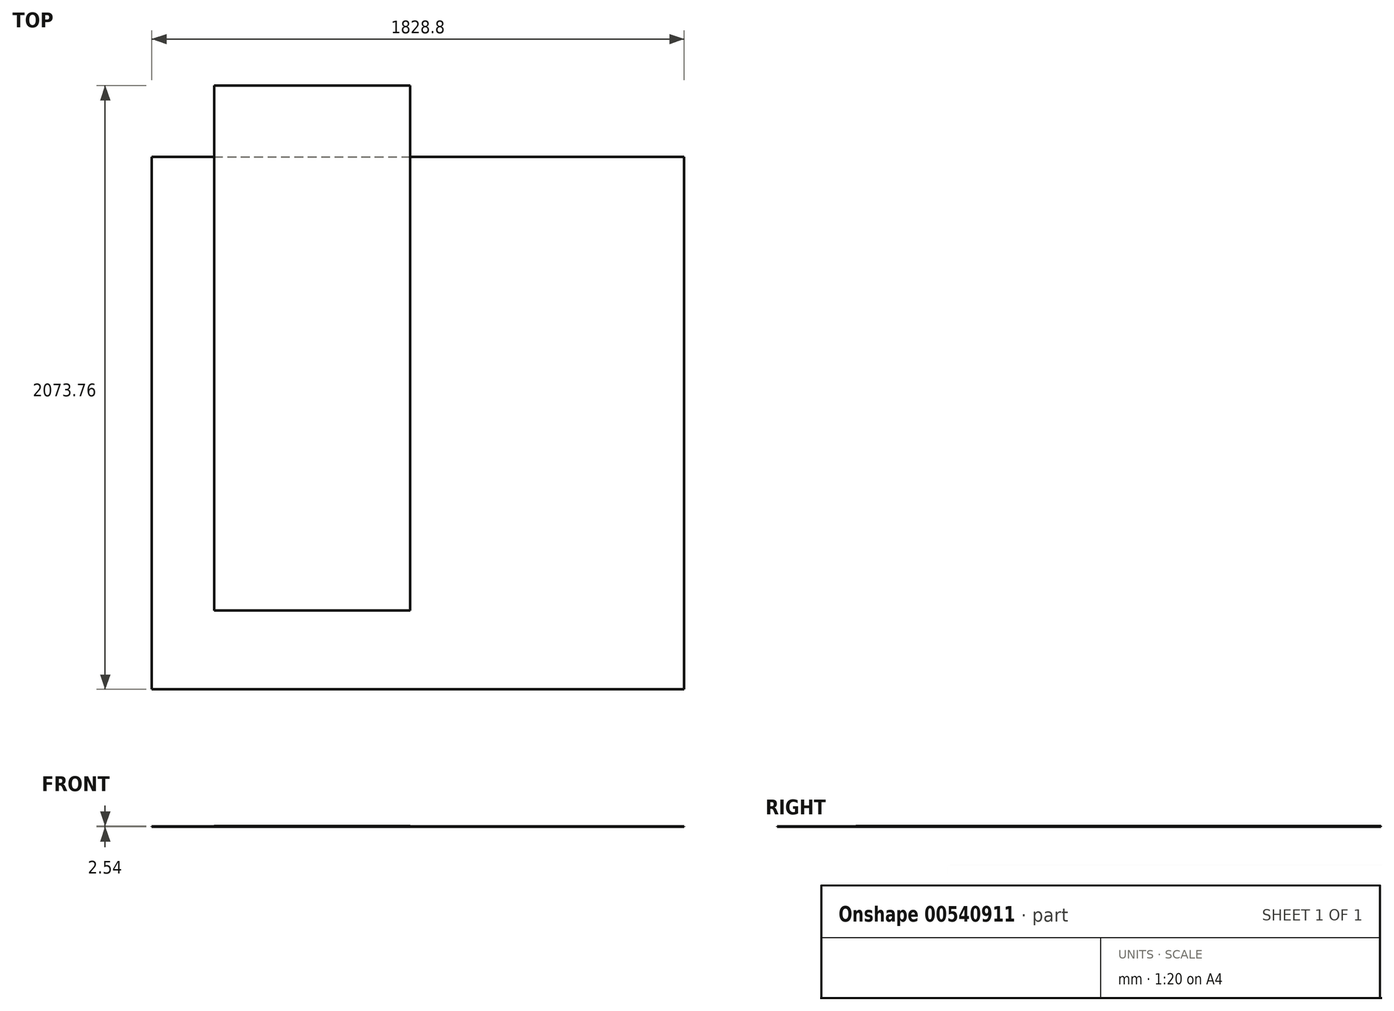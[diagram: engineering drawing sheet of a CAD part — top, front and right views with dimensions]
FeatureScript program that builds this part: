
annotation { "Feature Type Name" : "Feature", "Feature Type Description" : "" }
export const myFeature = defineFeature(function(context is Context, id is Id, definition is map)
    precondition{}
    {
        {
            var Q0;
            Q0=qCreatedBy(makeId("Top.planeOp"),FACE);
            var sketch = newSketch(context, id + "F0", { "sketchPlane" : qUnion([Q0])});
            skLineSegment(sketch, "E0.bottom", {"start": v(-914.4, 914.4) * mm, "end": v(914.4, 914.4) * mm});
            skLineSegment(sketch, "E0.top", {"start": v(-914.4, -914.4) * mm, "end": v(914.4, -914.4) * mm});
            skLineSegment(sketch, "E0.left", {"start": v(-914.4, 914.4) * mm, "end": v(-914.4, -914.4) * mm});
            skLineSegment(sketch, "E0.right", {"start": v(914.4, 914.4) * mm, "end": v(914.4, -914.4) * mm});
            skPoint(sketch, "E0.middle", {"position": v(0, 0) * mm});
            skSolve(sketch);
        }
        {
            var Q0;
            Q0 = qSketchRegion(id + "F0", true);
            extrude(context, id + "F1", {"entities" : qUnion([Q0]), "depth" : 1.27 * mm, "offsetDistance" : 25.4 * mm});
        }
        {
            var Q0;
            Q0=makeQuery(id+"F0.imprint","IMPRINT",FACE,{"disambiguationData":[TD([[makeQuery(id+"F0.imprint","IMPRINT",EDGE,{"derivedFrom":sQuery(id+"F0.wireOp",EDGE,"E0.bottom")}),-1.0]])]});
            var sketch = newSketch(context, id + "F2", { "sketchPlane" : qUnion([Q0])});
            skLineSegment(sketch, "E1.bottom", {"start": v(-700.42, 1159.36) * mm, "end": v(-27.32, 1159.36) * mm});
            skLineSegment(sketch, "E1.top", {"start": v(-700.42, -644.04) * mm, "end": v(-27.32, -644.04) * mm});
            skLineSegment(sketch, "E1.left", {"start": v(-700.42, 1159.36) * mm, "end": v(-700.42, -644.04) * mm});
            skLineSegment(sketch, "E1.right", {"start": v(-27.32, 1159.36) * mm, "end": v(-27.32, -644.04) * mm});
            skSolve(sketch);
        }
        {
            var Q0;
            Q0 = qSketchRegion(id + "F2", true);
            extrude(context, id + "F3", {"entities" : qUnion([Q0]), "depth" : 2.54 * mm, "offsetDistance" : 25.4 * mm});
        }
    });
